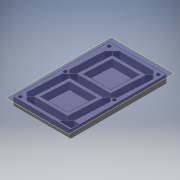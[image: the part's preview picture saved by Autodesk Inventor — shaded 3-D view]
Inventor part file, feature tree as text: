
AUTODESK INVENTOR PART (.ipt)
format: ipt  version: 2016 SP2 (Build 200236200, 236)  size: 308,224 bytes
history: native  units: mm
features: reference x11, extrude x4, sketch x4, plane x1
ambient origin geometry x8: Origin, YZ Plane, XZ Plane, XY Plane, X Axis, Y Axis, Z Axis, Center Point
bodies: Volumenkörper1 (feature_tree)
feature tree (20):
  plane  "Arbeitsebene1"
  extrude  "Extrusion1"  Depth=10.5mm
  extrude  "Extrusion2"  Depth=3.5mm
  extrude  "Extrusion3"  Depth=3.5mm
  extrude  "Extrusion4"  Depth=3.0mm
  sketch  "Skizze1"  dims[d0=10.5mm d1=0.0mm d2=3.5mm]
  reference  "Referenz1"
  sketch  "Skizze2"  dims[d3=3.5mm d4=3.5mm]
  sketch  "Skizze3"  dims[d5=3.5mm d6=3.5mm]
  reference  "Referenz2"
  reference  "Referenz3"
  reference  "Referenz4"
  reference  "Referenz5"
  reference  "Referenz6"
  sketch  "Skizze4"  dims[d7=3.5mm d8=3.5mm d9=3.5mm d10=3.5mm d11=3.5mm d12=3.5mm d13=3.5mm d14=3.5mm d15=3.5mm d16=3.5mm d17=3.5mm d18=1.7mm d19=1.7mm d20=1.7mm d21=1.7mm d22=1.7mm d23=1.7mm d24=1.7mm d25=1.7mm d26=1.7mm d27=1.7mm d28=1.7mm d29=1.7mm d30=1.7mm d31=1.7mm d32=1.7mm d33=1.7mm d34=1.7mm d35=1.7mm d36=0.8mm d37=0.8mm d38=0.8mm d39=0.8mm d40=0.8mm d41=0.8mm d42=0.8mm d43=0.8mm d44=0.8mm d45=0.8mm d46=0.8mm d47=0.8mm d48=0.8mm d49=0.8mm d50=0.8mm d51=0.0mm d52=3.0mm d53=0.0mm d54=3.0mm d55=0.0mm]
  reference  "Referenz7"
  reference  "Referenz8"
  reference  "Referenz9"
  reference  "Referenz10"
  reference  "Referenz11"
